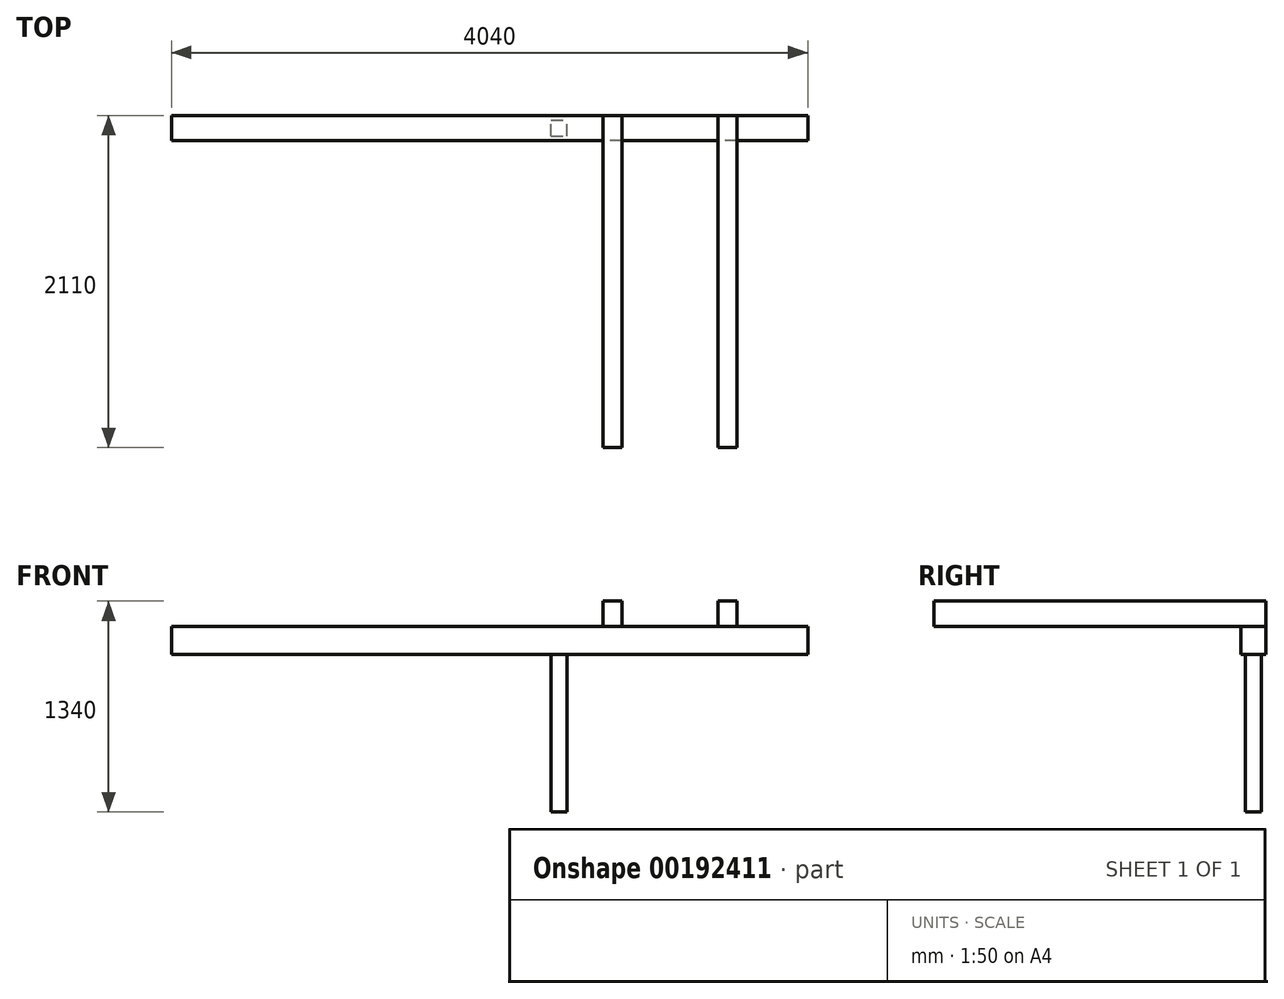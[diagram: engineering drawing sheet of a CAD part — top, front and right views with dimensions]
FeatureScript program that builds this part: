
annotation { "Feature Type Name" : "Feature", "Feature Type Description" : "" }
export const myFeature = defineFeature(function(context is Context, id is Id, definition is map)
    precondition{}
    {
        {
            var Q0;
            Q0=qCreatedBy(makeId("Top.planeOp"),FACE);
            var sketch = newSketch(context, id + "F0", { "sketchPlane" : qUnion([Q0])});
            skLineSegment(sketch, "E0.bottom", {"start": v(2020, -80) * mm, "end": v(-2020, -80) * mm});
            skLineSegment(sketch, "E0.top", {"start": v(2020, 80) * mm, "end": v(-2020, 80) * mm});
            skLineSegment(sketch, "E0.left", {"start": v(2020, -80) * mm, "end": v(2020, 80) * mm});
            skLineSegment(sketch, "E0.right", {"start": v(-2020, -80) * mm, "end": v(-2020, 80) * mm});
            skPoint(sketch, "E0.middle", {"position": v(0, 0) * mm});
            skLineSegment(sketch, "E1", {"start": v(1570, 80) * mm, "end": v(1570, -2030) * mm});
            skLineSegment(sketch, "E2", {"start": v(1570, -2030) * mm, "end": v(1450, -2030) * mm});
            skLineSegment(sketch, "E3", {"start": v(1450, -2030) * mm, "end": v(1450, 80) * mm});
            skLineSegment(sketch, "E4", {"start": v(840, 80) * mm, "end": v(840, -2030) * mm});
            skLineSegment(sketch, "E5", {"start": v(840, -2030) * mm, "end": v(720, -2030) * mm});
            skLineSegment(sketch, "E6", {"start": v(720, -2030) * mm, "end": v(720, 80) * mm});
            skSolve(sketch);
        }
        {
            var Q0;
            {var subQ0=sQuery(id+"F0.wireOp",EDGE,"E0.right");Q0=makeQuery(id+"F0.imprint","IMPRINT",FACE,{"disambiguationData":[TD([[makeQuery(id+"F0.imprint","IMPRINT",EDGE,{"derivedFrom":subQ0}),-1.0]])]});}
            var Q1;
            {var subQ0=sQuery(id+"F0.wireOp",EDGE,"E4");var subQ1=sQuery(id+"F0.wireOp",EDGE,"E0.bottom");var subQ2=makeQuery(id+"F0.imprint","INTERSECT",VERTEX,{"derivedFrom":[subQ1,subQ0]});Q1=makeQuery(id+"F0.imprint","IMPRINT",FACE,{"disambiguationData":[TD([[makeQuery(id+"F0.imprint","IMPRINT",EDGE,{"disambiguationData":[TD([[subQ2,-1.0]])],"derivedFrom":subQ1}),-1.0]])]});}
            var Q2;
            {var subQ0=sQuery(id+"F0.wireOp",EDGE,"E3");var subQ1=sQuery(id+"F0.wireOp",EDGE,"E0.bottom");var subQ2=makeQuery(id+"F0.imprint","INTERSECT",VERTEX,{"derivedFrom":[subQ1,subQ0]});Q2=makeQuery(id+"F0.imprint","IMPRINT",FACE,{"disambiguationData":[TD([[makeQuery(id+"F0.imprint","IMPRINT",EDGE,{"disambiguationData":[TD([[subQ2,-1.0]])],"derivedFrom":subQ1}),-1.0]])]});}
            var Q3;
            {var subQ0=sQuery(id+"F0.wireOp",EDGE,"E1");var subQ1=sQuery(id+"F0.wireOp",EDGE,"E0.bottom");var subQ2=makeQuery(id+"F0.imprint","INTERSECT",VERTEX,{"derivedFrom":[subQ1,subQ0]});Q3=makeQuery(id+"F0.imprint","IMPRINT",FACE,{"disambiguationData":[TD([[makeQuery(id+"F0.imprint","IMPRINT",EDGE,{"disambiguationData":[TD([[subQ2,-1.0]])],"derivedFrom":subQ1}),-1.0]])]});}
            var Q4;
            {var subQ0=sQuery(id+"F0.wireOp",EDGE,"E0.left");Q4=makeQuery(id+"F0.imprint","IMPRINT",FACE,{"disambiguationData":[TD([[makeQuery(id+"F0.imprint","IMPRINT",EDGE,{"derivedFrom":subQ0}),1.0]])]});}
            extrude(context, id + "F1", {"entities" : qUnion([Q0, Q1, Q2, Q3, Q4]), "oppositeDirection" : true, "depth" : 180 * mm});
        }
        {
            var Q0;
            {var subQ5=sQuery(id+"F0.wireOp",EDGE,"E5");Q0=makeQuery(id+"F0.imprint","IMPRINT",FACE,{"disambiguationData":[TD([[makeQuery(id+"F0.imprint","IMPRINT",EDGE,{"derivedFrom":subQ5}),-1.0]])]});}
            var Q1;
            {var subQ0=sQuery(id+"F0.wireOp",EDGE,"E4");var subQ1=sQuery(id+"F0.wireOp",EDGE,"E0.bottom");var subQ2=makeQuery(id+"F0.imprint","INTERSECT",VERTEX,{"derivedFrom":[subQ1,subQ0]});Q1=makeQuery(id+"F0.imprint","IMPRINT",FACE,{"disambiguationData":[TD([[makeQuery(id+"F0.imprint","IMPRINT",EDGE,{"disambiguationData":[TD([[subQ2,-1.0]])],"derivedFrom":subQ1}),-1.0]])]});}
            var Q2;
            {var subQ0=sQuery(id+"F0.wireOp",EDGE,"E1");var subQ1=sQuery(id+"F0.wireOp",EDGE,"E0.bottom");var subQ2=makeQuery(id+"F0.imprint","INTERSECT",VERTEX,{"derivedFrom":[subQ1,subQ0]});Q2=makeQuery(id+"F0.imprint","IMPRINT",FACE,{"disambiguationData":[TD([[makeQuery(id+"F0.imprint","IMPRINT",EDGE,{"disambiguationData":[TD([[subQ2,-1.0]])],"derivedFrom":subQ1}),-1.0]])]});}
            var Q3;
            {var subQ5=sQuery(id+"F0.wireOp",EDGE,"E2");Q3=makeQuery(id+"F0.imprint","IMPRINT",FACE,{"disambiguationData":[TD([[makeQuery(id+"F0.imprint","IMPRINT",EDGE,{"derivedFrom":subQ5}),-1.0]])]});}
            extrude(context, id + "F2", {"entities" : qUnion([Q0, Q1, Q2, Q3]), "operationType" : NewBodyOperationType.ADD, "depth" : 160 * mm});
        }
        {
            var Q0;
            Q0=makeQuery(id+"F1.opExtrude","CAP_FACE",FACE,{"disambiguationData":[OSD([sQuery(id+"F0.wireOp",EDGE,"E0.bottom"),sQuery(id+"F0.wireOp",EDGE,"E0.top"),sQuery(id+"F0.wireOp",EDGE,"E0.left"),sQuery(id+"F0.wireOp",EDGE,"E0.right")])],"isStart":false});
            var sketch = newSketch(context, id + "F3", { "sketchPlane" : qUnion([Q0])});
            skLineSegment(sketch, "E7.bottom", {"start": v(390.04, 50) * mm, "end": v(490, 50) * mm});
            skLineSegment(sketch, "E7.top", {"start": v(390.04, -50) * mm, "end": v(490, -50) * mm});
            skLineSegment(sketch, "E7.left", {"start": v(390.04, 50) * mm, "end": v(390.04, -50) * mm});
            skLineSegment(sketch, "E7.right", {"start": v(490, 50) * mm, "end": v(490, -50) * mm});
            skPoint(sketch, "E7.middle", {"position": v(440.02, 0) * mm});
            skPoint(sketch, "E7.middle.positionSnap0", {"position": v(2020, 0) * mm});
            skPoint(sketch, "E7.centerSnap0", {"position": v(2020, 0) * mm});
            skSolve(sketch);
        }
        {
            var Q0;
            Q0=makeQuery(id+"F3.imprint","IMPRINT",FACE,{"disambiguationData":[TD([[makeQuery(id+"F3.imprint","IMPRINT",EDGE,{"derivedFrom":sQuery(id+"F3.wireOp",EDGE,"E7.bottom")}),-1.0]])]});
            extrude(context, id + "F4", {"entities" : qUnion([Q0]), "operationType" : NewBodyOperationType.ADD, "depth" : 1000 * mm});
        }
    });
